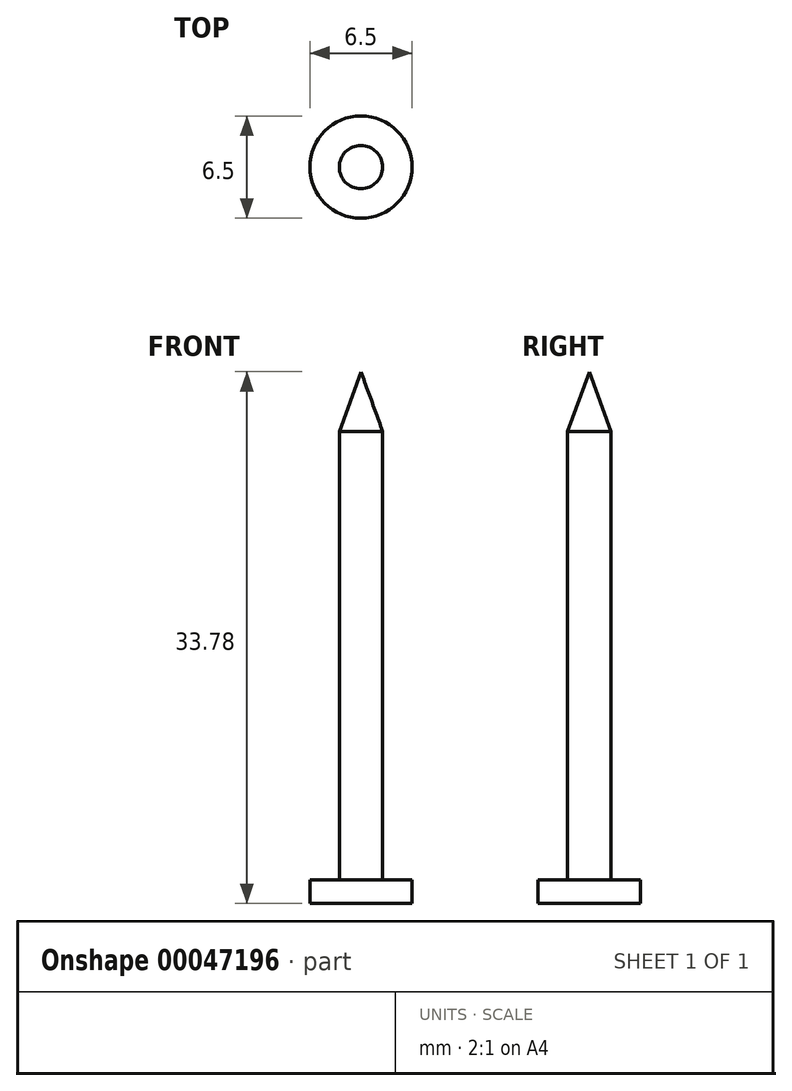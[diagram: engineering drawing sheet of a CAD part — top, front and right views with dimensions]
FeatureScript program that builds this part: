
annotation { "Feature Type Name" : "Feature", "Feature Type Description" : "" }
export const myFeature = defineFeature(function(context is Context, id is Id, definition is map)
    precondition{}
    {
        {
            var Q0;
            Q0=qCreatedBy(makeId("Top.planeOp"),FACE);
            var sketch = newSketch(context, id + "F0", { "sketchPlane" : qUnion([Q0])});
            skCircle(sketch, "E0", {"center": v(0, 0) * mm, "radius": 1.38 * mm});
            skCircle(sketch, "E1", {"center": v(0, 0) * mm, "radius": 3.25 * mm});
            skSolve(sketch);
        }
        {
            var Q0;
            Q0=makeQuery(id+"F0.imprint","IMPRINT",FACE,{"disambiguationData":[TD([[makeQuery(id+"F0.imprint","IMPRINT",EDGE,{"derivedFrom":sQuery(id+"F0.wireOp",EDGE,"E0")}),-1.0]])]});
            extrude(context, id + "F1", {"entities" : qUnion([Q0]), "depth" : 1.5 * mm});
        }
        {
            var Q0;
            Q0=makeQuery(id+"F0.imprint","IMPRINT",FACE,{"disambiguationData":[TD([[makeQuery(id+"F0.imprint","IMPRINT",EDGE,{"derivedFrom":sQuery(id+"F0.wireOp",EDGE,"E0")}),1.0]])]});
            extrude(context, id + "F2", {"entities" : qUnion([Q0]), "operationType" : NewBodyOperationType.ADD, "depth" : 30 * mm});
        }
        {
            var Q0;
            Q0=makeQuery(id+"F2.opExtrude","CAP_FACE",FACE,{"disambiguationData":[OSD([sQuery(id+"F0.wireOp",EDGE,"E0")])],"isStart":false});
            extrude(context, id + "F3", {"entities" : qUnion([Q0]), "operationType" : NewBodyOperationType.ADD, "depth" : 5 * mm, "hasDraft" : true, "draftAngle" : 20 * degree, "draftPullDirection" : true});
        }
    });
